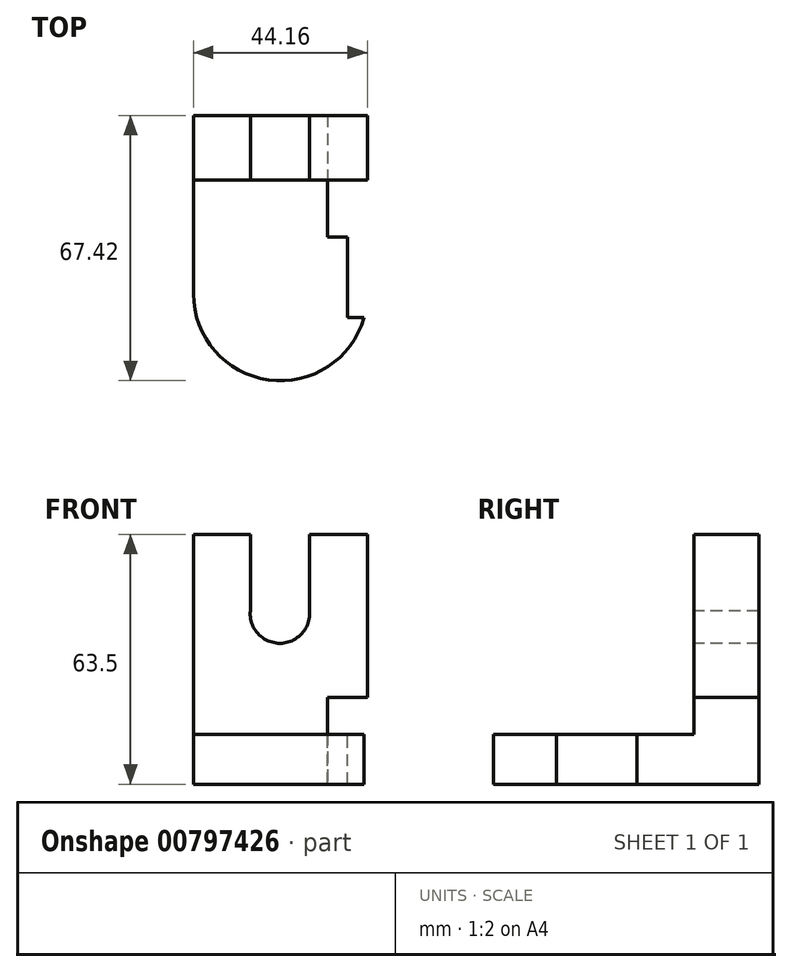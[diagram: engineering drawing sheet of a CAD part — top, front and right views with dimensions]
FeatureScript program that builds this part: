
annotation { "Feature Type Name" : "Feature", "Feature Type Description" : "" }
export const myFeature = defineFeature(function(context is Context, id is Id, definition is map)
    precondition{}
    {
        {
            var Q0;
            Q0=qCreatedBy(makeId("Top.planeOp"),FACE);
            var sketch = newSketch(context, id + "F0", { "sketchPlane" : qUnion([Q0])});
            skLineSegment(sketch, "E0.bottom", {"start": v(-22.08, 22.67) * mm, "end": v(22.08, 22.67) * mm});
            skLineSegment(sketch, "E0.top", {"start": v(-22.08, -22.67) * mm, "end": v(22.08, -22.67) * mm});
            skLineSegment(sketch, "E0.left", {"start": v(-22.08, 22.67) * mm, "end": v(-22.08, -22.67) * mm});
            skLineSegment(sketch, "E0.right", {"start": v(22.08, 22.67) * mm, "end": v(22.08, -22.67) * mm});
            skPoint(sketch, "E0.middle", {"position": v(0, 0) * mm});
            skArc(sketch, "E1", {"start": v(-22.08, -22.67) * mm, "mid": v(0, -44.75) * mm, "end": v(22.08, -22.67) * mm});
            skSolve(sketch);
        }
        {
            var Q0;
            Q0=makeQuery(id+"F0.imprint","IMPRINT",FACE,{"disambiguationData":[TD([[makeQuery(id+"F0.imprint","IMPRINT",EDGE,{"derivedFrom":sQuery(id+"F0.wireOp",EDGE,"E0.bottom")}),-1.0]])]});
            var Q1;
            Q1=makeQuery(id+"F0.imprint","IMPRINT",FACE,{"disambiguationData":[TD([[makeQuery(id+"F0.imprint","IMPRINT",EDGE,{"derivedFrom":sQuery(id+"F0.wireOp",EDGE,"E0.top")}),-1.0]])]});
            extrude(context, id + "F1", {"entities" : qUnion([Q0, Q1]), "depth" : 25.4 * mm, "offsetDistance" : 25.4 * mm});
        }
        {
            var Q0;
            Q0=makeQuery(id+"F1.opExtrude","CAP_FACE",FACE,{"disambiguationData":[OSD([sQuery(id+"F0.wireOp",EDGE,"E0.bottom"),sQuery(id+"F0.wireOp",EDGE,"E0.left"),sQuery(id+"F0.wireOp",EDGE,"E0.right"),sQuery(id+"F0.wireOp",EDGE,"E1")])],"isStart":false});
            extrude(context, id + "F2", {"entities" : qUnion([Q0]), "operationType" : NewBodyOperationType.REMOVE, "oppositeDirection" : true, "depth" : 12.7 * mm, "offsetDistance" : 25.4 * mm});
        }
        {
            var Q0;
            Q0=makeQuery(id+"F2.boolean.opBoolean","COPY",FACE,{"derivedFrom":makeQuery(id+"F2.opExtrude","CAP_FACE",FACE,{"disambiguationData":[OSD([sQuery(id+"F0.wireOp",EDGE,"E0.bottom"),sQuery(id+"F0.wireOp",EDGE,"E0.left"),sQuery(id+"F0.wireOp",EDGE,"E0.right"),sQuery(id+"F0.wireOp",EDGE,"E1")])],"isStart":false})});
            var sketch = newSketch(context, id + "F3", { "sketchPlane" : qUnion([Q0])});
            skLineSegment(sketch, "E2.bottom", {"start": v(-22.08, 22.67) * mm, "end": v(22.08, 22.67) * mm});
            skLineSegment(sketch, "E2.top", {"start": v(-22.08, 6.21) * mm, "end": v(22.08, 6.21) * mm});
            skLineSegment(sketch, "E2.left", {"start": v(-22.08, 22.67) * mm, "end": v(-22.08, 6.21) * mm});
            skLineSegment(sketch, "E2.right", {"start": v(22.08, 22.67) * mm, "end": v(22.08, 6.21) * mm});
            skSolve(sketch);
        }
        {
            var Q0;
            Q0=makeQuery(id+"F3.imprint","IMPRINT",FACE,{"disambiguationData":[TD([[makeQuery(id+"F3.imprint","IMPRINT",EDGE,{"derivedFrom":sQuery(id+"F3.wireOp",EDGE,"E2.bottom")}),-1.0]])]});
            extrude(context, id + "F4", {"entities" : qUnion([Q0]), "operationType" : NewBodyOperationType.ADD, "depth" : 50.8 * mm, "offsetDistance" : 25.4 * mm});
        }
        {
            var Q0;
            Q0=makeQuery(id+"F4.opExtrude","SWEPT_FACE",FACE,{"disambiguationData":[OSD([sQuery(id+"F3.wireOp",EDGE,"E2.top")])]});
            var sketch = newSketch(context, id + "F5", { "sketchPlane" : qUnion([Q0])});
            skLineSegment(sketch, "E3.bottom", {"start": v(-7.65, 63.5) * mm, "end": v(7.37, 63.5) * mm});
            skLineSegment(sketch, "E3.top", {"start": v(-7.65, 44.05) * mm, "end": v(7.37, 44.05) * mm});
            skLineSegment(sketch, "E3.left", {"start": v(-7.65, 63.5) * mm, "end": v(-7.65, 44.05) * mm});
            skLineSegment(sketch, "E3.right", {"start": v(7.37, 63.5) * mm, "end": v(7.37, 44.05) * mm});
            skArc(sketch, "E4", {"start": v(-7.65, 44.05) * mm, "mid": v(-0.14, 35.8) * mm, "end": v(7.37, 44.05) * mm});
            skSolve(sketch);
        }
        {
            var Q0;
            Q0=makeQuery(id+"F5.imprint","IMPRINT",FACE,{"disambiguationData":[TD([[makeQuery(id+"F5.imprint","IMPRINT",EDGE,{"derivedFrom":sQuery(id+"F5.wireOp",EDGE,"E3.bottom")}),-1.0]])]});
            var Q1;
            Q1=makeQuery(id+"F5.imprint","IMPRINT",FACE,{"disambiguationData":[TD([[makeQuery(id+"F5.imprint","IMPRINT",EDGE,{"derivedFrom":sQuery(id+"F5.wireOp",EDGE,"E3.top")}),-1.0]])]});
            extrude(context, id + "F6", {"entities" : qUnion([Q0, Q1]), "operationType" : NewBodyOperationType.REMOVE, "oppositeDirection" : true, "depth" : 50.8 * mm, "offsetDistance" : 25.4 * mm});
        }
        {
            var Q0;
            Q0=makeQuery(id+"F4.boolean.opBoolean","MERGE",FACE,{"derivedFrom":[makeQuery(id+"F1.opExtrude","SWEPT_FACE",FACE,{"disambiguationData":[OSD([sQuery(id+"F0.wireOp",EDGE,"E0.right")])]}),makeQuery(id+"F4.opExtrude","SWEPT_FACE",FACE,{"disambiguationData":[OSD([sQuery(id+"F3.wireOp",EDGE,"E2.right")])]})]});
            var sketch = newSketch(context, id + "F7", { "sketchPlane" : qUnion([Q0])});
            skPoint(sketch, "E5.oppositeSnap0", {"position": v(-8.23, 12.7) * mm});
            skLineSegment(sketch, "E5.bottom", {"start": v(22.67, 0) * mm, "end": v(-8.23, 0) * mm});
            skLineSegment(sketch, "E5.top", {"start": v(22.67, 22.1) * mm, "end": v(-8.23, 22.1) * mm});
            skLineSegment(sketch, "E5.left", {"start": v(22.67, 0) * mm, "end": v(22.67, 22.1) * mm});
            skLineSegment(sketch, "E5.right", {"start": v(-8.23, 0) * mm, "end": v(-8.23, 22.1) * mm});
            skSolve(sketch);
        }
        {
            var Q0;
            {var subQ1=sQuery(id+"F7.wireOp",EDGE,"E5.bottom");Q0=makeQuery(id+"F7.imprint","IMPRINT",FACE,{"disambiguationData":[TD([[makeQuery(id+"F7.imprint","IMPRINT",EDGE,{"derivedFrom":subQ1}),-1.0]])]});}
            extrude(context, id + "F8", {"entities" : qUnion([Q0]), "operationType" : NewBodyOperationType.REMOVE, "oppositeDirection" : true, "depth" : 10.16 * mm, "offsetDistance" : 25.4 * mm});
        }
        {
            var Q0;
            Q0=makeQuery(id+"F2.boolean.opBoolean","COPY",FACE,{"derivedFrom":makeQuery(id+"F2.opExtrude","CAP_FACE",FACE,{"disambiguationData":[OSD([sQuery(id+"F0.wireOp",EDGE,"E0.bottom"),sQuery(id+"F0.wireOp",EDGE,"E0.left"),sQuery(id+"F0.wireOp",EDGE,"E0.right"),sQuery(id+"F0.wireOp",EDGE,"E1")])],"isStart":false})});
            var sketch = newSketch(context, id + "F9", { "sketchPlane" : qUnion([Q0])});
            skLineSegment(sketch, "E6.bottom", {"start": v(17, -8.23) * mm, "end": v(30.76, -8.23) * mm});
            skLineSegment(sketch, "E6.top", {"start": v(17, -28.74) * mm, "end": v(30.76, -28.74) * mm});
            skLineSegment(sketch, "E6.left", {"start": v(17, -8.23) * mm, "end": v(17, -28.74) * mm});
            skLineSegment(sketch, "E6.right", {"start": v(30.76, -8.23) * mm, "end": v(30.76, -28.74) * mm});
            skSolve(sketch);
        }
        {
            var Q0;
            {var subQ2=sQuery(id+"F9.wireOp",EDGE,"E6.left");Q0=makeQuery(id+"F9.imprint","IMPRINT",FACE,{"disambiguationData":[TD([[makeQuery(id+"F9.imprint","IMPRINT",EDGE,{"derivedFrom":subQ2}),1.0]])]});}
            extrude(context, id + "F10", {"entities" : qUnion([Q0]), "operationType" : NewBodyOperationType.REMOVE, "oppositeDirection" : true, "depth" : 50.8 * mm, "offsetDistance" : 25.4 * mm});
        }
    });
